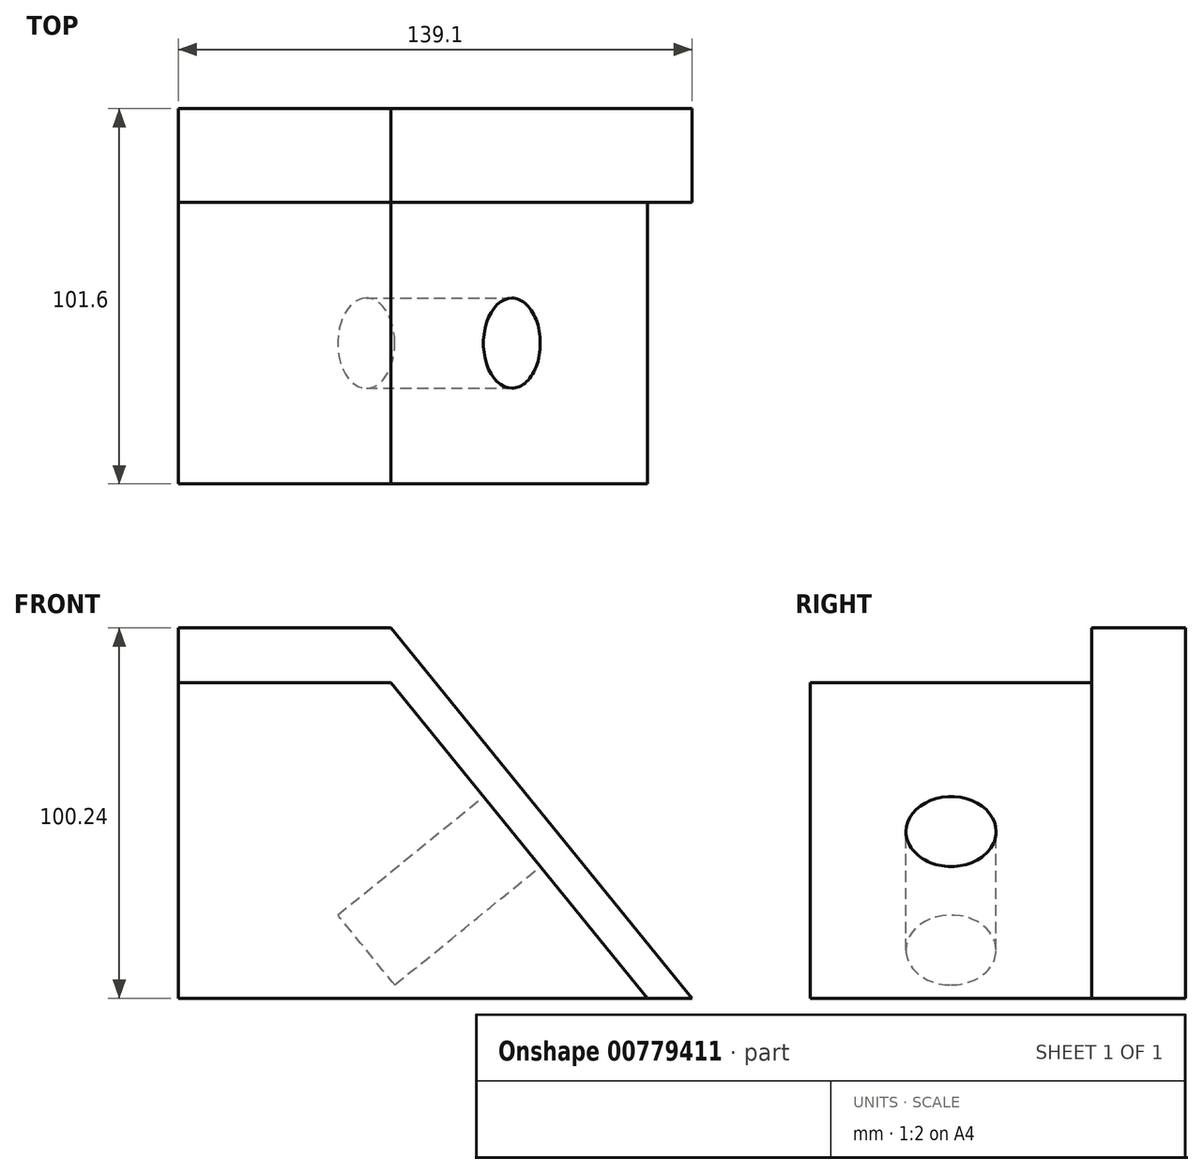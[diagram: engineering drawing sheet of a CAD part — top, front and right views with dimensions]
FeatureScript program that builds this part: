
annotation { "Feature Type Name" : "Feature", "Feature Type Description" : "" }
export const myFeature = defineFeature(function(context is Context, id is Id, definition is map)
    precondition{}
    {
        {
            var Q0;
            Q0=qCreatedBy(makeId("Front.planeOp"),FACE);
            var sketch = newSketch(context, id + "F0", { "sketchPlane" : qUnion([Q0])});
            skLineSegment(sketch, "E0", {"start": v(0, 28.4) * mm, "end": v(-57.55, 28.4) * mm});
            skLineSegment(sketch, "E1", {"start": v(-57.55, 28.4) * mm, "end": v(-57.55, -56.96) * mm});
            skLineSegment(sketch, "E2", {"start": v(-57.55, -56.96) * mm, "end": v(69.45, -56.96) * mm});
            skLineSegment(sketch, "E3", {"start": v(69.45, -56.96) * mm, "end": v(0, 28.4) * mm});
            skLineSegment(sketch, "E4", {"start": v(-57.55, 28.4) * mm, "end": v(-57.55, 43.28) * mm});
            skLineSegment(sketch, "E5", {"start": v(-57.55, 43.28) * mm, "end": v(0, 43.28) * mm});
            skLineSegment(sketch, "E6", {"start": v(0, 43.28) * mm, "end": v(81.55, -56.96) * mm});
            skLineSegment(sketch, "E7", {"start": v(69.45, -56.96) * mm, "end": v(81.55, -56.96) * mm});
            skSolve(sketch);
        }
        {
            var Q0;
            Q0=makeQuery(id+"F0.imprint","IMPRINT",FACE,{"disambiguationData":[TD([[makeQuery(id+"F0.imprint","IMPRINT",EDGE,{"derivedFrom":sQuery(id+"F0.wireOp",EDGE,"E0")}),1.0]])]});
            extrude(context, id + "F1", {"entities" : qUnion([Q0]), "depth" : 76.2 * mm, "offsetDistance" : 25.4 * mm});
        }
        {
            var Q0;
            Q0 = qSketchRegion(id + "F0", true);
            extrude(context, id + "F2", {"entities" : qUnion([Q0]), "operationType" : NewBodyOperationType.ADD, "oppositeDirection" : true, "depth" : 25.4 * mm, "offsetDistance" : 25.4 * mm});
        }
        {
            var Q0;
            Q0=makeQuery(id+"F1.opExtrude","SWEPT_FACE",FACE,{"disambiguationData":[OSD([sQuery(id+"F0.wireOp",EDGE,"E3")])]});
            var sketch = newSketch(context, id + "F3", { "sketchPlane" : qUnion([Q0])});
            skCircle(sketch, "E8", {"center": v(-38.1, -29.86) * mm, "radius": 12.2 * mm});
            skPoint(sketch, "E8.centerSnap0", {"position": v(-38.1, 22.03) * mm});
            skSolve(sketch);
        }
        {
            var Q0;
            Q0=makeQuery(id+"F3.imprint","IMPRINT",FACE,{"disambiguationData":[TD([[makeQuery(id+"F3.imprint","IMPRINT",EDGE,{"derivedFrom":sQuery(id+"F3.wireOp",EDGE,"E8")}),1.0]])]});
            extrude(context, id + "F4", {"entities" : qUnion([Q0]), "operationType" : NewBodyOperationType.REMOVE, "oppositeDirection" : true, "depth" : 50.8 * mm, "offsetDistance" : 25.4 * mm});
        }
    });
